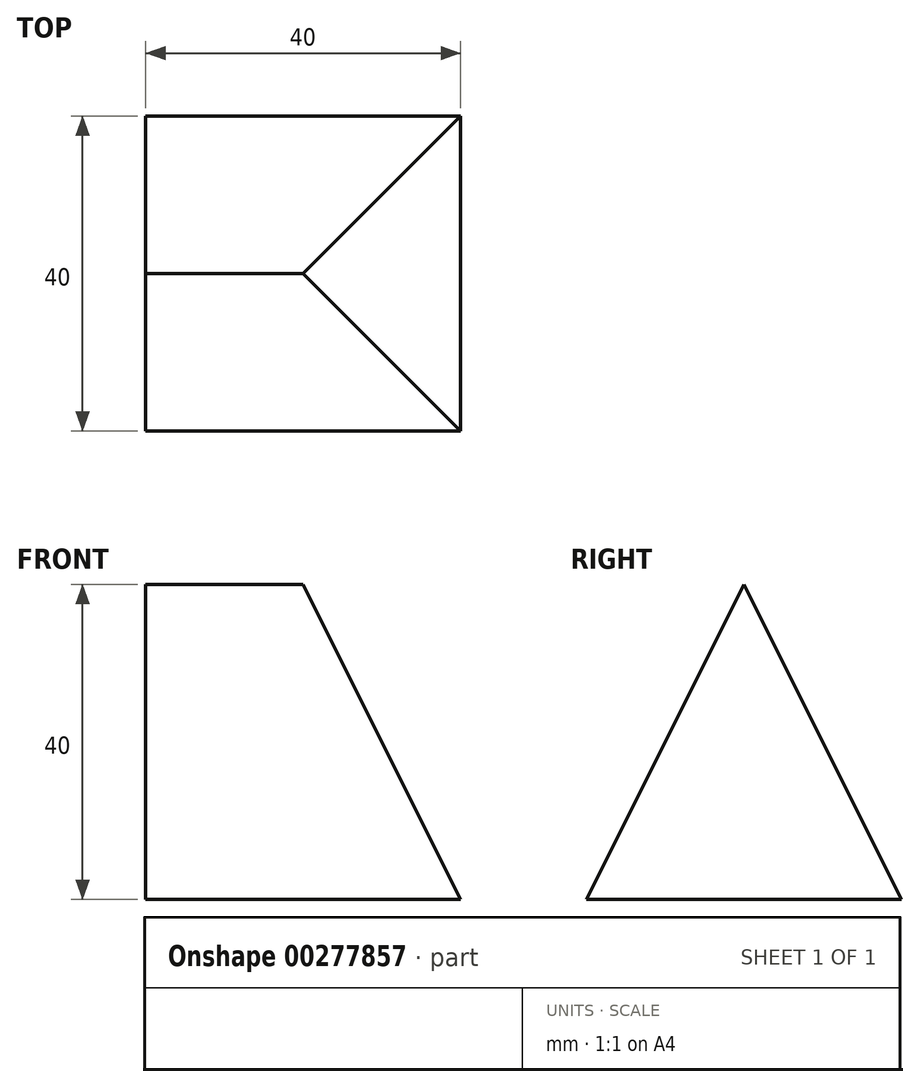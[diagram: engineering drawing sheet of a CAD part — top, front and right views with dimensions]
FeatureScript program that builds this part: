
annotation { "Feature Type Name" : "Feature", "Feature Type Description" : "" }
export const myFeature = defineFeature(function(context is Context, id is Id, definition is map)
    precondition{}
    {
        {
            var Q0;
            Q0=qCreatedBy(makeId("Right.planeOp"),FACE);
            var sketch = newSketch(context, id + "F0", { "sketchPlane" : qUnion([Q0])});
            skLineSegment(sketch, "E0.bottom", {"start": v(-20, 0) * mm, "end": v(20, 0) * mm});
            skLineSegment(sketch, "E1", {"start": v(-20, 0) * mm, "end": v(0, 40) * mm});
            skLineSegment(sketch, "E2", {"start": v(0, 40) * mm, "end": v(20, 0) * mm});
            skSolve(sketch);
        }
        {
            var Q0;
            Q0 = qSketchRegion(id + "F0", true);
            extrude(context, id + "F1", {"entities" : qUnion([Q0]), "depth" : 40 * mm});
        }
        {
            var Q0;
            Q0=qCreatedBy(makeId("Front.planeOp"),FACE);
            var sketch = newSketch(context, id + "F2", { "sketchPlane" : qUnion([Q0])});
            skLineSegment(sketch, "E3.0", {"start": v(40, 0) * mm, "end": v(40, 40) * mm});
            skLineSegment(sketch, "E4.0", {"start": v(40, 40) * mm, "end": v(20, 40) * mm});
            skLineSegment(sketch, "E5", {"start": v(40, 0) * mm, "end": v(20, 40) * mm});
            skPoint(sketch, "E6.orphan", {"position": v(0, 40) * mm});
            skSolve(sketch);
        }
        {
            var Q0;
            Q0 = qSketchRegion(id + "F2", true);
            extrude(context, id + "F3", {"entities" : qUnion([Q0]), "operationType" : NewBodyOperationType.REMOVE, "oppositeDirection" : true, "depth" : 40 * mm, "symmetric" : true});
        }
    });
